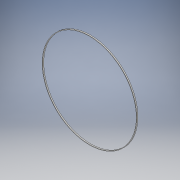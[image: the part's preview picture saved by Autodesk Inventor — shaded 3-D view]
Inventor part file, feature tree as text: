
AUTODESK INVENTOR PART (.ipt)
format: ipt  version: 2019 (Build 230136000, 136)  size: 105,472 bytes
history: native  units: mm
features: extrude x2, sketch x2
ambient origin geometry x8: Origin, YZ Plane, XZ Plane, XY Plane, X Axis, Y Axis, Z Axis, Center Point
bodies: Solid1 (feature_tree)
feature tree (4):
  extrude  "Extrusion1"  Depth=5.0mm TaperAngle=0.0deg
  extrude  "Extrusion2"  Depth=0.27mm TaperAngle=0.0deg
  sketch  "Sketch1"  dims[d0=407.0mm d1=5.0mm d2=0.0mm]
  sketch  "Sketch2"  dims[d3=403.0mm d4=0.27mm d5=0.0mm]
